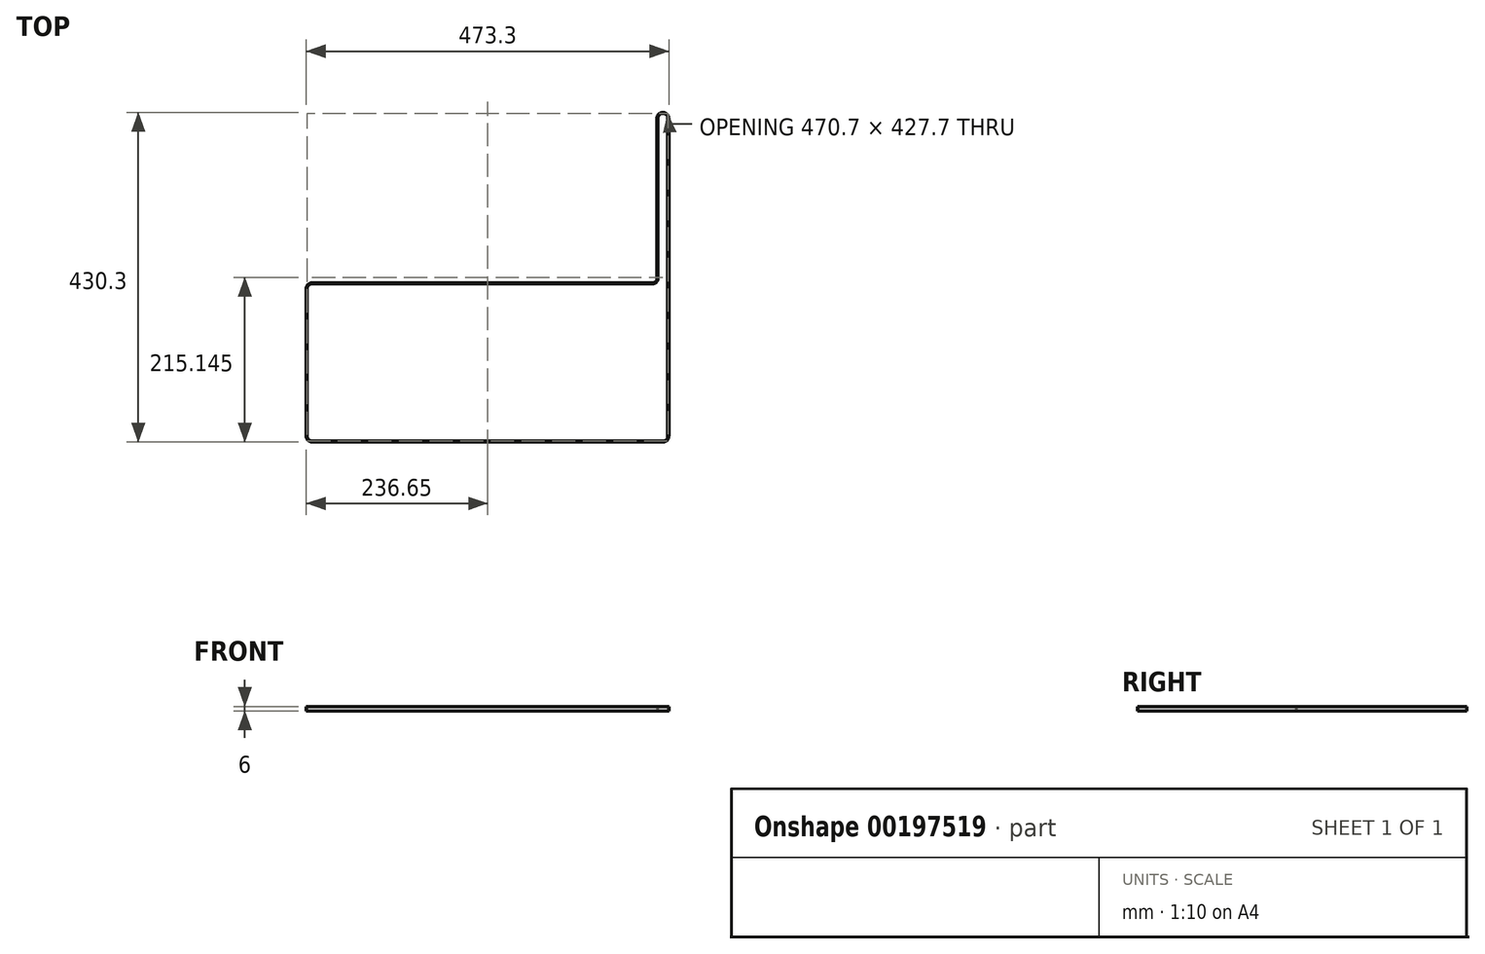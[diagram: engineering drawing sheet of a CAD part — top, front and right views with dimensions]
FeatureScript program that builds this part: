
annotation { "Feature Type Name" : "Feature", "Feature Type Description" : "" }
export const myFeature = defineFeature(function(context is Context, id is Id, definition is map)
    precondition{}
    {
        {
            var Q0;
            Q0=qCreatedBy(makeId("Top.planeOp"),FACE);
            var sketch = newSketch(context, id + "F0", { "sketchPlane" : qUnion([Q0])});
            skArc(sketch, "E0.1", {"start": v(3, 306.08) * mm, "mid": v(-3.5, 312.58) * mm, "end": v(-10, 306.08) * mm});
            skArc(sketch, "E0.4", {"start": v(-467.7, -108.62) * mm, "mid": v(-465.8, -113.22) * mm, "end": v(-461.2, -115.12) * mm});
            skArc(sketch, "E0.5", {"start": v(-3.5, -115.12) * mm, "mid": v(1.09, -113.22) * mm, "end": v(3, -108.62) * mm});
            skArc(sketch, "E1", {"start": v(-461.2, 90.23) * mm, "mid": v(-465.8, 88.32) * mm, "end": v(-467.7, 83.73) * mm});
            skArc(sketch, "E2", {"start": v(-16.5, 90.23) * mm, "mid": v(-11.91, 92.13) * mm, "end": v(-10, 96.73) * mm});
            skLineSegment(sketch, "E3", {"start": v(-10, 306.08) * mm, "end": v(-10, 96.73) * mm});
            skLineSegment(sketch, "E4", {"start": v(-16.5, 90.23) * mm, "end": v(-244.86, 90.23) * mm});
            skLineSegment(sketch, "E5", {"start": v(3, 306.08) * mm, "end": v(3, -108.62) * mm});
            skLineSegment(sketch, "E6", {"start": v(-461.2, -115.12) * mm, "end": v(-3.5, -115.12) * mm});
            skLineSegment(sketch, "E7", {"start": v(-467.7, -108.62) * mm, "end": v(-467.7, 83.73) * mm});
            skLineSegment(sketch, "E8", {"start": v(-461.2, 90.23) * mm, "end": v(-244.86, 90.23) * mm});
            skArc(sketch, "E9.0", {"start": v(4.3, 306.08) * mm, "mid": v(-3.5, 313.88) * mm, "end": v(-11.3, 306.08) * mm});
            skArc(sketch, "E10.0", {"start": v(-16.5, 91.53) * mm, "mid": v(-12.83, 93.05) * mm, "end": v(-11.3, 96.73) * mm});
            skArc(sketch, "E11.0", {"start": v(-461.2, 91.53) * mm, "mid": v(-466.73, 89.24) * mm, "end": v(-469, 83.73) * mm});
            skArc(sketch, "E12.0", {"start": v(-469, -108.62) * mm, "mid": v(-466.73, -114.14) * mm, "end": v(-461.2, -116.42) * mm});
            skArc(sketch, "E13.0", {"start": v(-3.5, -116.42) * mm, "mid": v(2, -114.14) * mm, "end": v(4.3, -108.62) * mm});
            skLineSegment(sketch, "E14", {"start": v(4.3, 306.08) * mm, "end": v(4.3, -108.62) * mm});
            skLineSegment(sketch, "E15", {"start": v(-3.5, -116.42) * mm, "end": v(-461.2, -116.42) * mm});
            skLineSegment(sketch, "E16", {"start": v(-469, -108.62) * mm, "end": v(-469, 83.73) * mm});
            skLineSegment(sketch, "E17", {"start": v(-461.2, 91.53) * mm, "end": v(-441.14, 91.53) * mm});
            skLineSegment(sketch, "E18", {"start": v(-16.5, 91.53) * mm, "end": v(-441.14, 91.53) * mm});
            skLineSegment(sketch, "E19", {"start": v(-11.3, 96.73) * mm, "end": v(-11.3, 306.08) * mm});
            skSolve(sketch);
        }
        {
            var Q0;
            Q0=qSketchRegion(id+"F0",true);
            extrude(context, id + "F1", {"entities" : qUnion([Q0]), "depth" : 6 * mm});
        }
    });
